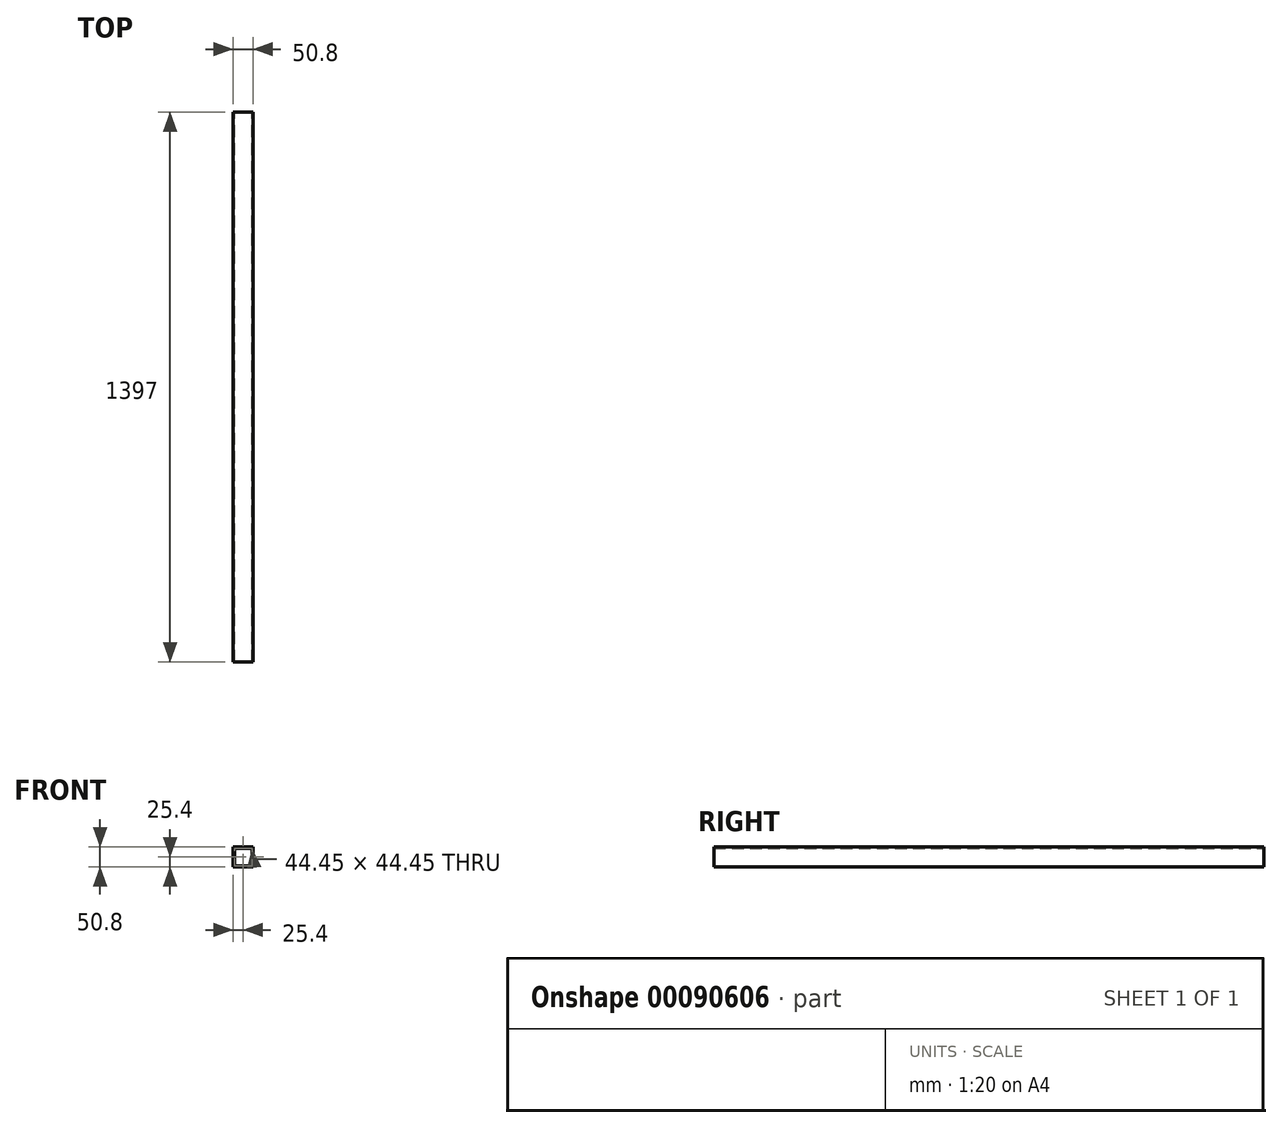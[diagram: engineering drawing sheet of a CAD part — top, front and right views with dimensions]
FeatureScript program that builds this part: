
annotation { "Feature Type Name" : "Feature", "Feature Type Description" : "" }
export const myFeature = defineFeature(function(context is Context, id is Id, definition is map)
    precondition{}
    {
        {
            var Q0;
            Q0=qCreatedBy(makeId("Front.planeOp"),FACE);
            var sketch = newSketch(context, id + "F0", { "sketchPlane" : qUnion([Q0])});
            skLineSegment(sketch, "E0.bottom", {"start": v(25.4, 25.4) * mm, "end": v(-25.4, 25.4) * mm});
            skLineSegment(sketch, "E0.top", {"start": v(25.4, -25.4) * mm, "end": v(-25.4, -25.4) * mm});
            skLineSegment(sketch, "E0.left", {"start": v(25.4, 25.4) * mm, "end": v(25.4, -25.4) * mm});
            skLineSegment(sketch, "E0.right", {"start": v(-25.4, 25.4) * mm, "end": v(-25.4, -25.4) * mm});
            skPoint(sketch, "E0.middle", {"position": v(0, 0) * mm});
            skLineSegment(sketch, "E1.bottom", {"start": v(22.23, 22.23) * mm, "end": v(-22.23, 22.23) * mm});
            skLineSegment(sketch, "E1.top", {"start": v(22.23, -22.23) * mm, "end": v(-22.23, -22.23) * mm});
            skLineSegment(sketch, "E1.left", {"start": v(22.23, 22.23) * mm, "end": v(22.23, -22.23) * mm});
            skLineSegment(sketch, "E1.right", {"start": v(-22.23, 22.23) * mm, "end": v(-22.23, -22.23) * mm});
            skSolve(sketch);
        }
        {
            var Q0;
            Q0 = qSketchRegion(id + "F0", true);
            extrude(context, id + "F1", {"entities" : qUnion([Q0]), "endBound" : BoundingType.SYMMETRIC, "depth" : 1397 * mm});
        }
    });
